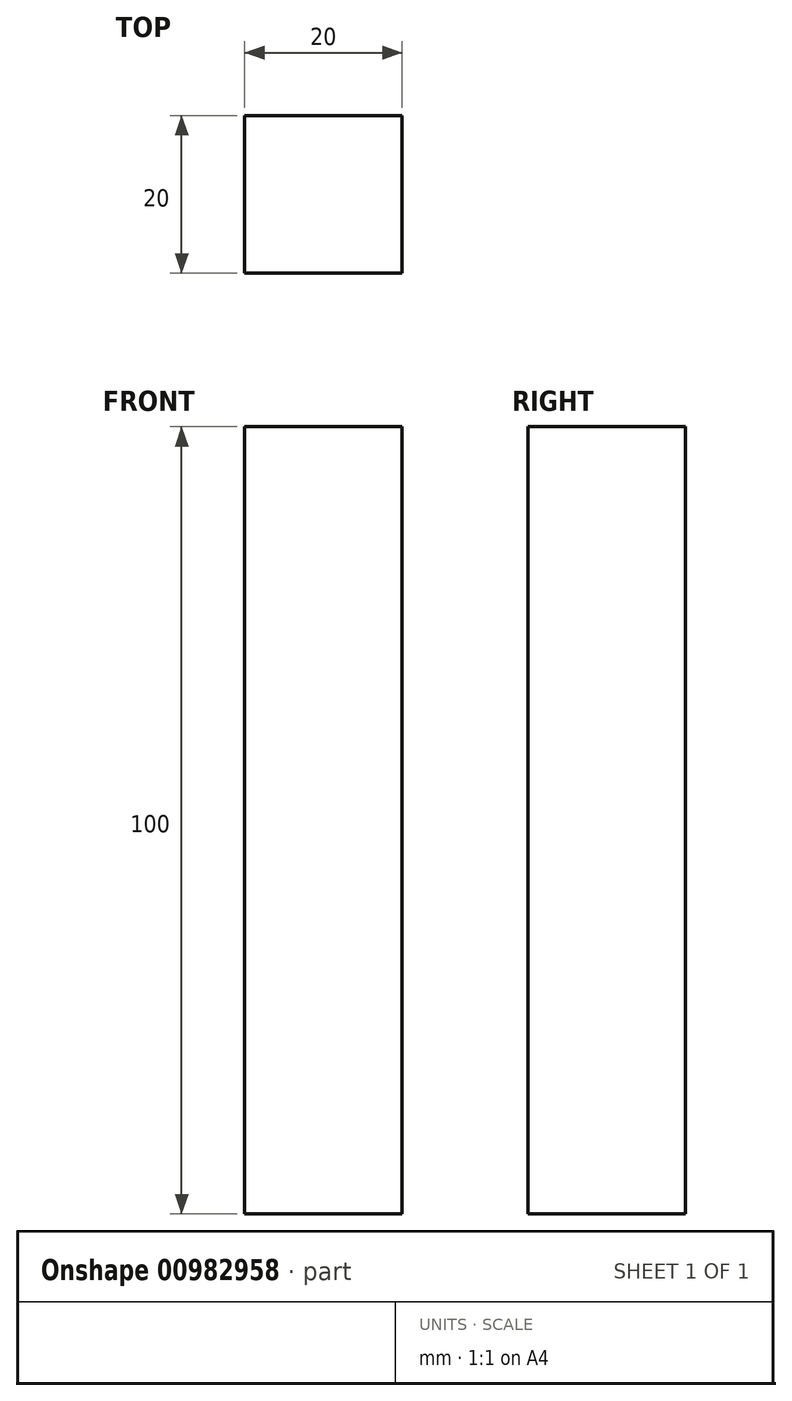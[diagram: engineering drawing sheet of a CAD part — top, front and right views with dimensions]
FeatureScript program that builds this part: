
annotation { "Feature Type Name" : "Feature", "Feature Type Description" : "" }
export const myFeature = defineFeature(function(context is Context, id is Id, definition is map)
    precondition{}
    {
        {
            var Q0;
            Q0=qCreatedBy(makeId("Top.planeOp"),FACE);
            var sketch = newSketch(context, id + "F0", { "sketchPlane" : qUnion([Q0])});
            skLineSegment(sketch, "E0.bottom", {"start": v(-12.2, 10.23) * mm, "end": v(7.8, 10.23) * mm});
            skLineSegment(sketch, "E0.top", {"start": v(-12.2, -9.77) * mm, "end": v(7.8, -9.77) * mm});
            skLineSegment(sketch, "E0.left", {"start": v(-12.2, 10.23) * mm, "end": v(-12.2, -9.77) * mm});
            skLineSegment(sketch, "E0.right", {"start": v(7.8, 10.23) * mm, "end": v(7.8, -9.77) * mm});
            skSolve(sketch);
        }
        {
            var Q0;
            Q0 = qSketchRegion(id + "F0", true);
            extrude(context, id + "F1", {"entities" : qUnion([Q0]), "depth" : 100 * mm, "offsetDistance" : 25 * mm});
        }
    });
